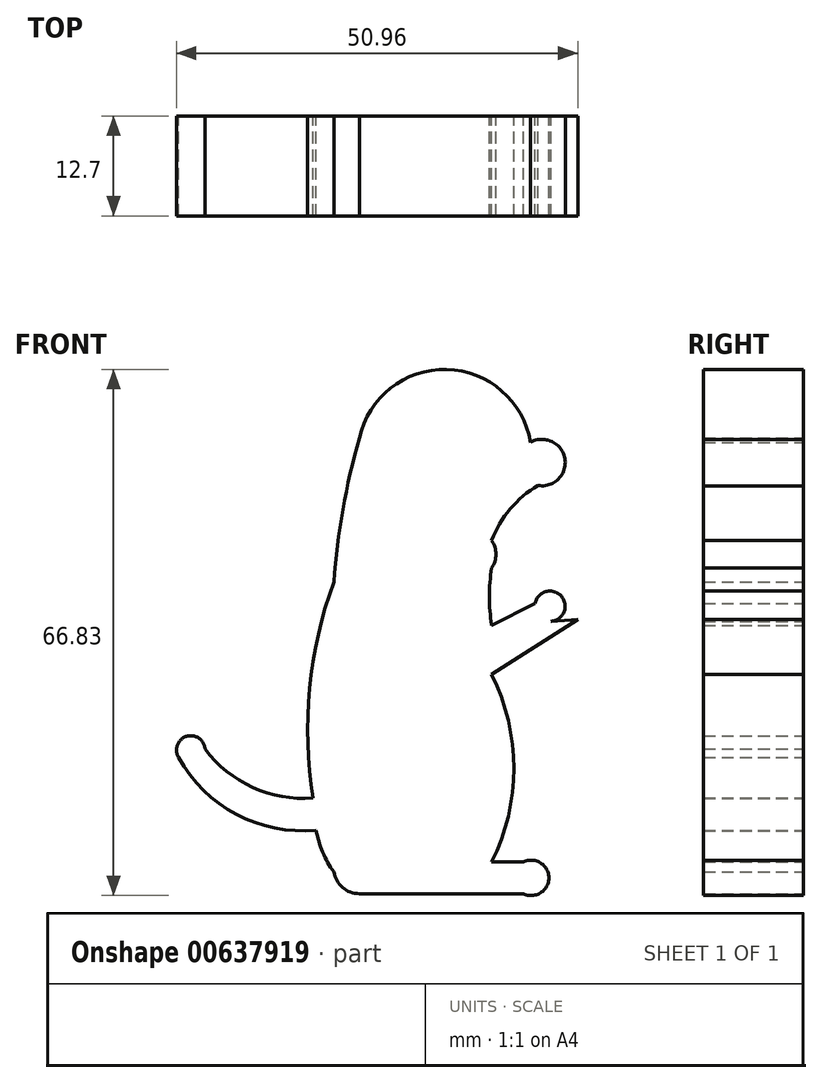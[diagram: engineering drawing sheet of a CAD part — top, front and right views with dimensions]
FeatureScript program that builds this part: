
annotation { "Feature Type Name" : "Feature", "Feature Type Description" : "" }
export const myFeature = defineFeature(function(context is Context, id is Id, definition is map)
    precondition{}
    {
        {
            var Q0;
            Q0=qCreatedBy(makeId("Front.planeOp"),FACE);
            var sketch = newSketch(context, id + "F0", { "sketchPlane" : qUnion([Q0])});
            skArc(sketch, "E0", {"start": v(44.7, 49.27) * mm, "mid": v(34.05, 58.52) * mm, "end": v(22.96, 49.8) * mm});
            skArc(sketch, "E1", {"start": v(39.77, 33.3) * mm, "mid": v(39.48, 29.67) * mm, "end": v(39.77, 26.04) * mm});
            skLineSegment(sketch, "E2", {"start": v(39.77, 26.04) * mm, "end": v(45.3, 28.8) * mm});
            skArc(sketch, "E3", {"start": v(47.3, 26.54) * mm, "mid": v(48.61, 29.73) * mm, "end": v(45.3, 28.8) * mm});
            skLineSegment(sketch, "E4", {"start": v(47.3, 26.54) * mm, "end": v(50.7, 26.75) * mm});
            skLineSegment(sketch, "E5", {"start": v(50.7, 26.75) * mm, "end": v(39.77, 19.77) * mm});
            skArc(sketch, "E6", {"start": v(39.77, -4.05) * mm, "mid": v(42.57, 7.86) * mm, "end": v(39.77, 19.77) * mm});
            skLineSegment(sketch, "E7", {"start": v(39.77, -4.05) * mm, "end": v(43.79, -4.05) * mm});
            skLineSegment(sketch, "E8", {"start": v(39.52, -8.07) * mm, "end": v(43.79, -8.07) * mm});
            skArc(sketch, "E9", {"start": v(43.79, -8.07) * mm, "mid": v(47.03, -6.06) * mm, "end": v(43.79, -4.05) * mm});
            skLineSegment(sketch, "E10", {"start": v(39.52, -8.07) * mm, "end": v(22.96, -8.07) * mm});
            skArc(sketch, "E11", {"start": v(19.71, -5.3) * mm, "mid": v(20.83, -7.28) * mm, "end": v(22.96, -8.07) * mm});
            skPoint(sketch, "E12.start.orphan", {"position": v(15.83, 17.96) * mm});
            skArc(sketch, "E13", {"start": v(39.77, 33.3) * mm, "mid": v(40.32, 35.06) * mm, "end": v(39.77, 36.82) * mm});
            skPoint(sketch, "E14.end.orphan", {"position": v(47.55, 49.27) * mm});
            skPoint(sketch, "E15.end.orphan", {"position": v(0, 5.98) * mm});
            skPoint(sketch, "E16.end.orphan", {"position": v(19.71, 0) * mm});
            skArc(sketch, "E17", {"start": v(17.47, 0) * mm, "mid": v(18.3, -2.78) * mm, "end": v(19.71, -5.3) * mm});
            skArc(sketch, "E18", {"start": v(0, 9.26) * mm, "mid": v(7.35, 2.01) * mm, "end": v(17.47, 0) * mm});
            skArc(sketch, "E19", {"start": v(3.36, 10.3) * mm, "mid": v(9.42, 5.44) * mm, "end": v(17.06, 4.07) * mm});
            skArc(sketch, "E20", {"start": v(3.36, 10.3) * mm, "mid": v(1.02, 11.92) * mm, "end": v(0, 9.26) * mm});
            skPoint(sketch, "E21.end.orphan", {"position": v(19.71, 31.55) * mm});
            skPoint(sketch, "E21.start.orphan", {"position": v(19.71, 39.5) * mm});
            skPoint(sketch, "E22.start.orphan", {"position": v(19.71, 20.8) * mm});
            skPoint(sketch, "E23.end.orphan", {"position": v(19.71, 33.66) * mm});
            skPoint(sketch, "E24.start.orphan", {"position": v(15.93, 20.8) * mm});
            skArc(sketch, "E25", {"start": v(19.71, 31.55) * mm, "mid": v(16.65, 17.98) * mm, "end": v(17.06, 4.07) * mm});
            skArc(sketch, "E26", {"start": v(22.96, 49.8) * mm, "mid": v(20.87, 40.76) * mm, "end": v(19.71, 31.55) * mm});
            skPoint(sketch, "E27.start.orphan", {"position": v(47.55, 44.1) * mm});
            skArc(sketch, "E28", {"start": v(45.66, 43.79) * mm, "mid": v(42.13, 40.8) * mm, "end": v(39.77, 36.82) * mm});
            skArc(sketch, "E29", {"start": v(45.66, 43.79) * mm, "mid": v(49.07, 47.2) * mm, "end": v(44.7, 49.27) * mm});
            skSolve(sketch);
        }
        {
            var Q0;
            Q0 = qSketchRegion(id + "F0", true);
            extrude(context, id + "F1", {"entities" : qUnion([Q0]), "depth" : 12.7 * mm, "offsetDistance" : 25.4 * mm});
        }
    });
